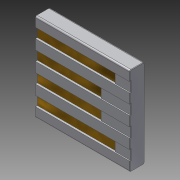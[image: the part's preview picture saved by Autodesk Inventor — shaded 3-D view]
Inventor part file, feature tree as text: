
AUTODESK INVENTOR PART (.ipt)
format: ipt  version: 2015 (Build 190159000, 159)  size: 217,088 bytes
history: native  units: in
note: dims shown in document units (in); Inventor stores cm internally (conversion verified against a paired STEP export)
features: extrude x4, sketch x4, mirror x2, fillet x2, pattern_linear x1
ambient origin geometry x8: Origin, YZ Plane, XZ Plane, XY Plane, X Axis, Y Axis, Z Axis, Center Point
bodies: Solid1 (feature_tree)
feature tree (13):
  extrude  "Extrusion1"  Depth=0.48in
  extrude  "Extrusion2"  Depth=0.24in
  mirror  "Mirror1"
  extrude  "Extrusion3"  Depth=0.4in
  pattern_linear  "Rectangular Pattern1"  Spacing1=0.05in  [1 undecoded]
  extrude  "Extrusion4"  Depth=0.05in
  mirror  "Mirror2"
  fillet  "Fillet1"  Radius=0.05in
  fillet  "Fillet2"  Radius=0.33in
  sketch  "Sketch1"  dims[d0=0.45in d1=0.48in]
  sketch  "Sketch2"  dims[d2=0.225in d3=0.24in]
  sketch  "Sketch4"  dims[d4=0.075in d5=0.0in d6=0.4in]
  sketch  "Sketch5"  dims[d7=0.05in d8=0.05in d9=0.05in d10=0.05in d11=0.33in d12=0.025in d13=0.0in d16=0.2in d17=0.05in d18=0.005in d19=0.0in d20=1.5748in d22=0.1in d23=0.015in d24=0.0in d25=0.0075in d26=0.0025in]
note: 1 required parameter value undecoded (feature->parameter linkage not recoverable at this tier; creation-order binding heuristic only, values carry confidence <= 0.55)
